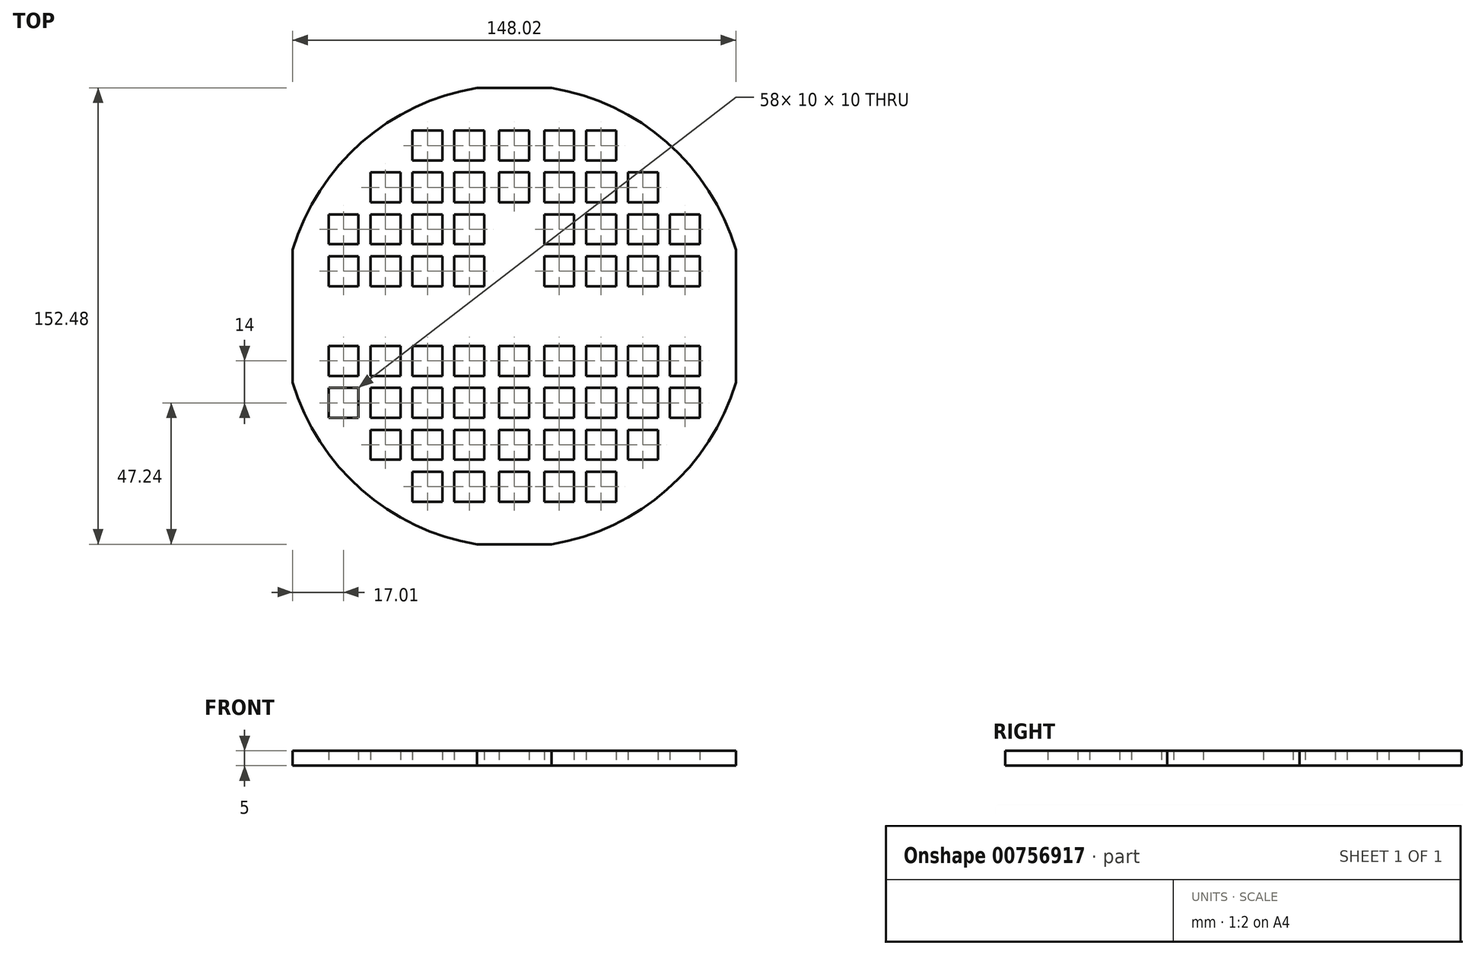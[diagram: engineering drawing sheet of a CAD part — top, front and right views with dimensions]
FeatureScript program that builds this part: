
annotation { "Feature Type Name" : "Feature", "Feature Type Description" : "" }
export const myFeature = defineFeature(function(context is Context, id is Id, definition is map)
    precondition{}
    {
        {
            var Q0;
            Q0=qCreatedBy(makeId("Top.planeOp"),FACE);
            var sketch = newSketch(context, id + "F0", { "sketchPlane" : qUnion([Q0])});
            skArc(sketch, "E0", {"start": v(-74, -22.14) * mm, "mid": v(-51, -58.03) * mm, "end": v(-12.45, -76.24) * mm});
            skLineSegment(sketch, "E1.bottom", {"start": v(10, 20) * mm, "end": v(20, 20) * mm});
            skLineSegment(sketch, "E1.top", {"start": v(10, 10) * mm, "end": v(20, 10) * mm});
            skLineSegment(sketch, "E1.left", {"start": v(10, 20) * mm, "end": v(10, 10) * mm});
            skLineSegment(sketch, "E1.right", {"start": v(20, 20) * mm, "end": v(20, 10) * mm});
            skPoint(sketch, "E1.middle", {"position": v(15, 15) * mm});
            skLineSegment(sketch, "E2.0.1.0", {"start": v(10, 24) * mm, "end": v(20, 24) * mm});
            skLineSegment(sketch, "E2.0.1.1", {"start": v(20, 34) * mm, "end": v(20, 24) * mm});
            skLineSegment(sketch, "E2.0.1.2", {"start": v(10, 34) * mm, "end": v(20, 34) * mm});
            skPoint(sketch, "E2.0.1.3", {"position": v(15, 29) * mm});
            skLineSegment(sketch, "E2.0.1.4", {"start": v(10, 34) * mm, "end": v(10, 24) * mm});
            skLineSegment(sketch, "E2.0.2.0", {"start": v(10, 38) * mm, "end": v(20, 38) * mm});
            skLineSegment(sketch, "E2.0.2.1", {"start": v(20, 48) * mm, "end": v(20, 38) * mm});
            skLineSegment(sketch, "E2.0.2.2", {"start": v(10, 48) * mm, "end": v(20, 48) * mm});
            skPoint(sketch, "E2.0.2.3", {"position": v(15, 43) * mm});
            skLineSegment(sketch, "E2.0.2.4", {"start": v(10, 48) * mm, "end": v(10, 38) * mm});
            skLineSegment(sketch, "E2.0.3.0", {"start": v(10, 52) * mm, "end": v(20, 52) * mm});
            skLineSegment(sketch, "E2.0.3.1", {"start": v(20, 62) * mm, "end": v(20, 52) * mm});
            skLineSegment(sketch, "E2.0.3.2", {"start": v(10, 62) * mm, "end": v(20, 62) * mm});
            skPoint(sketch, "E2.0.3.3", {"position": v(15, 57) * mm});
            skLineSegment(sketch, "E2.0.3.4", {"start": v(10, 62) * mm, "end": v(10, 52) * mm});
            skLineSegment(sketch, "E2.1.0.0", {"start": v(24, 10) * mm, "end": v(34, 10) * mm});
            skLineSegment(sketch, "E2.1.0.1", {"start": v(34, 20) * mm, "end": v(34, 10) * mm});
            skLineSegment(sketch, "E2.1.0.2", {"start": v(24, 20) * mm, "end": v(34, 20) * mm});
            skPoint(sketch, "E2.1.0.3", {"position": v(29, 15) * mm});
            skLineSegment(sketch, "E2.1.0.4", {"start": v(24, 20) * mm, "end": v(24, 10) * mm});
            skLineSegment(sketch, "E2.1.1.0", {"start": v(24, 24) * mm, "end": v(34, 24) * mm});
            skLineSegment(sketch, "E2.1.1.1", {"start": v(34, 34) * mm, "end": v(34, 24) * mm});
            skLineSegment(sketch, "E2.1.1.2", {"start": v(24, 34) * mm, "end": v(34, 34) * mm});
            skPoint(sketch, "E2.1.1.3", {"position": v(29, 29) * mm});
            skLineSegment(sketch, "E2.1.1.4", {"start": v(24, 34) * mm, "end": v(24, 24) * mm});
            skLineSegment(sketch, "E2.1.2.0", {"start": v(24, 38) * mm, "end": v(34, 38) * mm});
            skLineSegment(sketch, "E2.1.2.1", {"start": v(34, 48) * mm, "end": v(34, 38) * mm});
            skLineSegment(sketch, "E2.1.2.2", {"start": v(24, 48) * mm, "end": v(34, 48) * mm});
            skPoint(sketch, "E2.1.2.3", {"position": v(29, 43) * mm});
            skLineSegment(sketch, "E2.1.2.4", {"start": v(24, 48) * mm, "end": v(24, 38) * mm});
            skLineSegment(sketch, "E2.1.3.0", {"start": v(24, 52) * mm, "end": v(34, 52) * mm});
            skLineSegment(sketch, "E2.1.3.1", {"start": v(34, 62) * mm, "end": v(34, 52) * mm});
            skLineSegment(sketch, "E2.1.3.2", {"start": v(24, 62) * mm, "end": v(34, 62) * mm});
            skPoint(sketch, "E2.1.3.3", {"position": v(29, 57) * mm});
            skLineSegment(sketch, "E2.1.3.4", {"start": v(24, 62) * mm, "end": v(24, 52) * mm});
            skLineSegment(sketch, "E2.2.0.0", {"start": v(38, 10) * mm, "end": v(48, 10) * mm});
            skLineSegment(sketch, "E2.2.0.1", {"start": v(48, 20) * mm, "end": v(48, 10) * mm});
            skLineSegment(sketch, "E2.2.0.2", {"start": v(38, 20) * mm, "end": v(48, 20) * mm});
            skPoint(sketch, "E2.2.0.3", {"position": v(43, 15) * mm});
            skLineSegment(sketch, "E2.2.0.4", {"start": v(38, 20) * mm, "end": v(38, 10) * mm});
            skLineSegment(sketch, "E2.2.1.0", {"start": v(38, 24) * mm, "end": v(48, 24) * mm});
            skLineSegment(sketch, "E2.2.1.1", {"start": v(48, 34) * mm, "end": v(48, 24) * mm});
            skLineSegment(sketch, "E2.2.1.2", {"start": v(38, 34) * mm, "end": v(48, 34) * mm});
            skPoint(sketch, "E2.2.1.3", {"position": v(43, 29) * mm});
            skLineSegment(sketch, "E2.2.1.4", {"start": v(38, 34) * mm, "end": v(38, 24) * mm});
            skLineSegment(sketch, "E2.2.2.0", {"start": v(38, 38) * mm, "end": v(48, 38) * mm});
            skLineSegment(sketch, "E2.2.2.1", {"start": v(48, 48) * mm, "end": v(48, 38) * mm});
            skLineSegment(sketch, "E2.2.2.2", {"start": v(38, 48) * mm, "end": v(48, 48) * mm});
            skPoint(sketch, "E2.2.2.3", {"position": v(43, 43) * mm});
            skLineSegment(sketch, "E2.2.2.4", {"start": v(38, 48) * mm, "end": v(38, 38) * mm});
            skLineSegment(sketch, "E2.3.0.0", {"start": v(52, 10) * mm, "end": v(62, 10) * mm});
            skLineSegment(sketch, "E2.3.0.1", {"start": v(62, 20) * mm, "end": v(62, 10) * mm});
            skLineSegment(sketch, "E2.3.0.2", {"start": v(52, 20) * mm, "end": v(62, 20) * mm});
            skPoint(sketch, "E2.3.0.3", {"position": v(57, 15) * mm});
            skLineSegment(sketch, "E2.3.0.4", {"start": v(52, 20) * mm, "end": v(52, 10) * mm});
            skLineSegment(sketch, "E2.3.1.0", {"start": v(52, 24) * mm, "end": v(62, 24) * mm});
            skLineSegment(sketch, "E2.3.1.1", {"start": v(62, 34) * mm, "end": v(62, 24) * mm});
            skLineSegment(sketch, "E2.3.1.2", {"start": v(52, 34) * mm, "end": v(62, 34) * mm});
            skPoint(sketch, "E2.3.1.3", {"position": v(57, 29) * mm});
            skLineSegment(sketch, "E2.3.1.4", {"start": v(52, 34) * mm, "end": v(52, 24) * mm});
            skLineSegment(sketch, "E2.direction1", {"start": v(10, 10) * mm, "end": v(24, 10) * mm, "construction": true});
            skLineSegment(sketch, "E2.direction2", {"start": v(10, 10) * mm, "end": v(10, 24) * mm, "construction": true});
            skLineSegment(sketch, "E3.MirrorCS", {"start": v(34, -20) * mm, "end": v(34, -10) * mm});
            skLineSegment(sketch, "E4.MirrorCS", {"start": v(10, -10) * mm, "end": v(20, -10) * mm});
            skLineSegment(sketch, "E5.MirrorCS", {"start": v(10, -20) * mm, "end": v(10, -10) * mm});
            skLineSegment(sketch, "E6.MirrorCS", {"start": v(48, -20) * mm, "end": v(48, -10) * mm});
            skLineSegment(sketch, "E7.MirrorCS", {"start": v(62, -34) * mm, "end": v(62, -24) * mm});
            skLineSegment(sketch, "E8.MirrorCS", {"start": v(24, -62) * mm, "end": v(34, -62) * mm});
            skLineSegment(sketch, "E9.MirrorCS", {"start": v(48, -34) * mm, "end": v(48, -24) * mm});
            skPoint(sketch, "E10.MirrorP", {"position": v(29, -29) * mm});
            skPoint(sketch, "E11.MirrorP", {"position": v(57, -15) * mm});
            skPoint(sketch, "E12.MirrorP", {"position": v(29, -43) * mm});
            skLineSegment(sketch, "E13.MirrorCS", {"start": v(38, -10) * mm, "end": v(48, -10) * mm});
            skLineSegment(sketch, "E14.MirrorCS", {"start": v(52, -24) * mm, "end": v(62, -24) * mm});
            skLineSegment(sketch, "E15.MirrorCS", {"start": v(24, -34) * mm, "end": v(24, -24) * mm});
            skLineSegment(sketch, "E16.MirrorCS", {"start": v(24, -10) * mm, "end": v(34, -10) * mm});
            skLineSegment(sketch, "E17.MirrorCS", {"start": v(38, -34) * mm, "end": v(38, -24) * mm});
            skLineSegment(sketch, "E18.MirrorCS", {"start": v(24, -48) * mm, "end": v(24, -38) * mm});
            skPoint(sketch, "E19.MirrorP", {"position": v(29, -15) * mm});
            skLineSegment(sketch, "E20.MirrorCS", {"start": v(52, -20) * mm, "end": v(52, -10) * mm});
            skLineSegment(sketch, "E21.MirrorCS", {"start": v(10, -62) * mm, "end": v(10, -52) * mm});
            skPoint(sketch, "E22.MirrorP", {"position": v(15, -57) * mm});
            skPoint(sketch, "E23.MirrorP", {"position": v(57, -29) * mm});
            skPoint(sketch, "E24.MirrorP", {"position": v(15, -15) * mm});
            skLineSegment(sketch, "E25.MirrorCS", {"start": v(10, -20) * mm, "end": v(20, -20) * mm});
            skLineSegment(sketch, "E26.MirrorCS", {"start": v(20, -62) * mm, "end": v(20, -52) * mm});
            skPoint(sketch, "E27.MirrorP", {"position": v(29, -57) * mm});
            skLineSegment(sketch, "E28.MirrorCS", {"start": v(24, -48) * mm, "end": v(34, -48) * mm});
            skLineSegment(sketch, "E29.MirrorCS", {"start": v(10, -52) * mm, "end": v(20, -52) * mm});
            skLineSegment(sketch, "E30.MirrorCS", {"start": v(52, -34) * mm, "end": v(62, -34) * mm});
            skLineSegment(sketch, "E31.MirrorCS", {"start": v(38, -20) * mm, "end": v(48, -20) * mm});
            skLineSegment(sketch, "E32.MirrorCS", {"start": v(24, -20) * mm, "end": v(34, -20) * mm});
            skLineSegment(sketch, "E33.MirrorCS", {"start": v(24, -20) * mm, "end": v(24, -10) * mm});
            skLineSegment(sketch, "E34.MirrorCS", {"start": v(10, -62) * mm, "end": v(20, -62) * mm});
            skLineSegment(sketch, "E35.MirrorCS", {"start": v(52, -10) * mm, "end": v(62, -10) * mm});
            skLineSegment(sketch, "E36.MirrorCS", {"start": v(52, -34) * mm, "end": v(52, -24) * mm});
            skLineSegment(sketch, "E37.MirrorCS", {"start": v(38, -20) * mm, "end": v(38, -10) * mm});
            skLineSegment(sketch, "E38.MirrorCS", {"start": v(24, -52) * mm, "end": v(34, -52) * mm});
            skLineSegment(sketch, "E39.MirrorCS", {"start": v(24, -62) * mm, "end": v(24, -52) * mm});
            skArc(sketch, "E40.MirrorC", {"start": v(-74, 22.14) * mm, "mid": v(-51, 58.03) * mm, "end": v(-12.45, 76.24) * mm});
            skLineSegment(sketch, "E41.MirrorCS", {"start": v(34, -48) * mm, "end": v(34, -38) * mm});
            skPoint(sketch, "E42.MirrorP", {"position": v(43, -15) * mm});
            skPoint(sketch, "E43.MirrorP", {"position": v(15, -29) * mm});
            skLineSegment(sketch, "E44.MirrorCS", {"start": v(48, -48) * mm, "end": v(48, -38) * mm});
            skLineSegment(sketch, "E45.MirrorCS", {"start": v(38, -48) * mm, "end": v(38, -38) * mm});
            skLineSegment(sketch, "E46.MirrorCS", {"start": v(24, -24) * mm, "end": v(34, -24) * mm});
            skLineSegment(sketch, "E47.MirrorCS", {"start": v(10, -10) * mm, "end": v(24, -10) * mm, "construction": true});
            skLineSegment(sketch, "E48.MirrorCS", {"start": v(62, -20) * mm, "end": v(62, -10) * mm});
            skLineSegment(sketch, "E49.MirrorCS", {"start": v(38, -24) * mm, "end": v(48, -24) * mm});
            skLineSegment(sketch, "E50.MirrorCS", {"start": v(20, -20) * mm, "end": v(20, -10) * mm});
            skLineSegment(sketch, "E51.MirrorCS", {"start": v(10, -24) * mm, "end": v(20, -24) * mm});
            skLineSegment(sketch, "E52.MirrorCS", {"start": v(24, -34) * mm, "end": v(34, -34) * mm});
            skLineSegment(sketch, "E53.MirrorCS", {"start": v(20, -34) * mm, "end": v(20, -24) * mm});
            skLineSegment(sketch, "E54.MirrorCS", {"start": v(38, -38) * mm, "end": v(48, -38) * mm});
            skLineSegment(sketch, "E55.MirrorCS", {"start": v(52, -20) * mm, "end": v(62, -20) * mm});
            skLineSegment(sketch, "E56.MirrorCS", {"start": v(34, -62) * mm, "end": v(34, -52) * mm});
            skPoint(sketch, "E57.MirrorP", {"position": v(15, -43) * mm});
            skPoint(sketch, "E58.MirrorP", {"position": v(43, -43) * mm});
            skLineSegment(sketch, "E59.MirrorCS", {"start": v(10, -34) * mm, "end": v(20, -34) * mm});
            skLineSegment(sketch, "E60.MirrorCS", {"start": v(20, -48) * mm, "end": v(20, -38) * mm});
            skLineSegment(sketch, "E61.MirrorCS", {"start": v(38, -34) * mm, "end": v(48, -34) * mm});
            skLineSegment(sketch, "E62.MirrorCS", {"start": v(10, -10) * mm, "end": v(10, -24) * mm, "construction": true});
            skLineSegment(sketch, "E63.MirrorCS", {"start": v(38, -48) * mm, "end": v(48, -48) * mm});
            skLineSegment(sketch, "E64.MirrorCS", {"start": v(10, -34) * mm, "end": v(10, -24) * mm});
            skLineSegment(sketch, "E65.MirrorCS", {"start": v(34, -34) * mm, "end": v(34, -24) * mm});
            skPoint(sketch, "E66.MirrorP", {"position": v(43, -29) * mm});
            skLineSegment(sketch, "E67.MirrorCS", {"start": v(10, -38) * mm, "end": v(20, -38) * mm});
            skLineSegment(sketch, "E68.MirrorCS", {"start": v(10, -48) * mm, "end": v(10, -38) * mm});
            skLineSegment(sketch, "E69.MirrorCS", {"start": v(24, -38) * mm, "end": v(34, -38) * mm});
            skLineSegment(sketch, "E70.MirrorCS", {"start": v(10, -48) * mm, "end": v(20, -48) * mm});
            skLineSegment(sketch, "E71.MirrorCS", {"start": v(-34, 20) * mm, "end": v(-34, 10) * mm});
            skLineSegment(sketch, "E72.MirrorCS", {"start": v(-10, -20) * mm, "end": v(-10, -10) * mm});
            skLineSegment(sketch, "E73.MirrorCS", {"start": v(-10, -10) * mm, "end": v(-20, -10) * mm});
            skLineSegment(sketch, "E74.MirrorCS", {"start": v(-10, 10) * mm, "end": v(-20, 10) * mm});
            skLineSegment(sketch, "E75.MirrorCS", {"start": v(-48, -20) * mm, "end": v(-48, -10) * mm});
            skLineSegment(sketch, "E76.MirrorCS", {"start": v(-10, 20) * mm, "end": v(-10, 10) * mm});
            skLineSegment(sketch, "E77.MirrorCS", {"start": v(-20, -20) * mm, "end": v(-20, -10) * mm});
            skPoint(sketch, "E78.MirrorP", {"position": v(-15, 15) * mm});
            skPoint(sketch, "E79.MirrorP", {"position": v(-29, -15) * mm});
            skLineSegment(sketch, "E80.MirrorCS", {"start": v(-34, -62) * mm, "end": v(-34, -52) * mm});
            skLineSegment(sketch, "E81.MirrorCS", {"start": v(-48, 20) * mm, "end": v(-48, 10) * mm});
            skLineSegment(sketch, "E82.MirrorCS", {"start": v(-62, 34) * mm, "end": v(-62, 24) * mm});
            skLineSegment(sketch, "E83.MirrorCS", {"start": v(-38, -34) * mm, "end": v(-38, -24) * mm});
            skLineSegment(sketch, "E84.MirrorCS", {"start": v(-24, -52) * mm, "end": v(-34, -52) * mm});
            skPoint(sketch, "E85.MirrorP", {"position": v(-43, 29) * mm});
            skPoint(sketch, "E86.MirrorP", {"position": v(-43, -43) * mm});
            skLineSegment(sketch, "E87.MirrorCS", {"start": v(-10, -52) * mm, "end": v(-20, -52) * mm});
            skLineSegment(sketch, "E88.MirrorCS", {"start": v(-10, -10) * mm, "end": v(-24, -10) * mm, "construction": true});
            skLineSegment(sketch, "E89.MirrorCS", {"start": v(-34, -34) * mm, "end": v(-34, -24) * mm});
            skLineSegment(sketch, "E90.MirrorCS", {"start": v(-24, 38) * mm, "end": v(-34, 38) * mm});
            skLineSegment(sketch, "E91.MirrorCS", {"start": v(-38, 38) * mm, "end": v(-48, 38) * mm});
            skLineSegment(sketch, "E92.MirrorCS", {"start": v(-52, -20) * mm, "end": v(-62, -20) * mm});
            skLineSegment(sketch, "E93.MirrorCS", {"start": v(-38, 10) * mm, "end": v(-48, 10) * mm});
            skLineSegment(sketch, "E94.MirrorCS", {"start": v(-52, 24) * mm, "end": v(-62, 24) * mm});
            skLineSegment(sketch, "E95.MirrorCS", {"start": v(-24, -10) * mm, "end": v(-34, -10) * mm});
            skLineSegment(sketch, "E96.MirrorCS", {"start": v(-38, -20) * mm, "end": v(-38, -10) * mm});
            skLineSegment(sketch, "E97.MirrorCS", {"start": v(-24, 10) * mm, "end": v(-34, 10) * mm});
            skPoint(sketch, "E98.MirrorP", {"position": v(-43, 15) * mm});
            skPoint(sketch, "E99.MirrorP", {"position": v(-15, -43) * mm});
            skLineSegment(sketch, "E100.MirrorCS", {"start": v(-24, -48) * mm, "end": v(-34, -48) * mm});
            skLineSegment(sketch, "E101.MirrorCS", {"start": v(-24, -24) * mm, "end": v(-34, -24) * mm});
            skLineSegment(sketch, "E102.MirrorCS", {"start": v(-10, -34) * mm, "end": v(-10, -24) * mm});
            skLineSegment(sketch, "E103.MirrorCS", {"start": v(-24, 34) * mm, "end": v(-24, 24) * mm});
            skLineSegment(sketch, "E104.MirrorCS", {"start": v(-38, 34) * mm, "end": v(-38, 24) * mm});
            skPoint(sketch, "E105.MirrorP", {"position": v(-29, -43) * mm});
            skLineSegment(sketch, "E106.MirrorCS", {"start": v(-24, 62) * mm, "end": v(-24, 52) * mm});
            skLineSegment(sketch, "E107.MirrorCS", {"start": v(-52, 20) * mm, "end": v(-52, 10) * mm});
            skLineSegment(sketch, "E108.MirrorCS", {"start": v(-24, -34) * mm, "end": v(-24, -24) * mm});
            skLineSegment(sketch, "E109.MirrorCS", {"start": v(-52, -34) * mm, "end": v(-52, -24) * mm});
            skLineSegment(sketch, "E110.MirrorCS", {"start": v(-10, 62) * mm, "end": v(-10, 52) * mm});
            skPoint(sketch, "E111.MirrorP", {"position": v(-29, 57) * mm});
            skPoint(sketch, "E112.MirrorP", {"position": v(-15, -29) * mm});
            skLineSegment(sketch, "E113.MirrorCS", {"start": v(-20, -62) * mm, "end": v(-20, -52) * mm});
            skLineSegment(sketch, "E114.MirrorCS", {"start": v(-38, -48) * mm, "end": v(-38, -38) * mm});
            skLineSegment(sketch, "E115.MirrorCS", {"start": v(-38, -48) * mm, "end": v(-48, -48) * mm});
            skLineSegment(sketch, "E116.MirrorCS", {"start": v(-24, 34) * mm, "end": v(-34, 34) * mm});
            skLineSegment(sketch, "E117.MirrorCS", {"start": v(-38, 34) * mm, "end": v(-48, 34) * mm});
            skLineSegment(sketch, "E118.MirrorCS", {"start": v(-34, -20) * mm, "end": v(-34, -10) * mm});
            skPoint(sketch, "E119.MirrorP", {"position": v(-57, -15) * mm});
            skLineSegment(sketch, "E120.MirrorCS", {"start": v(-38, -38) * mm, "end": v(-48, -38) * mm});
            skLineSegment(sketch, "E121.MirrorCS", {"start": v(-10, 48) * mm, "end": v(-10, 38) * mm});
            skLineSegment(sketch, "E122.MirrorCS", {"start": v(-10, 48) * mm, "end": v(-20, 48) * mm});
            skLineSegment(sketch, "E123.MirrorCS", {"start": v(-20, 48) * mm, "end": v(-20, 38) * mm});
            skLineSegment(sketch, "E124.MirrorCS", {"start": v(-10, 38) * mm, "end": v(-20, 38) * mm});
            skLineSegment(sketch, "E125.MirrorCS", {"start": v(-10, 34) * mm, "end": v(-10, 24) * mm});
            skLineSegment(sketch, "E126.MirrorCS", {"start": v(-10, 24) * mm, "end": v(-20, 24) * mm});
            skLineSegment(sketch, "E127.MirrorCS", {"start": v(-10, 20) * mm, "end": v(-20, 20) * mm});
            skLineSegment(sketch, "E128.MirrorCS", {"start": v(-10, 52) * mm, "end": v(-20, 52) * mm});
            skLineSegment(sketch, "E129.MirrorCS", {"start": v(-20, -34) * mm, "end": v(-20, -24) * mm});
            skLineSegment(sketch, "E130.MirrorCS", {"start": v(-10, -10) * mm, "end": v(-10, -24) * mm, "construction": true});
            skLineSegment(sketch, "E131.MirrorCS", {"start": v(-24, 62) * mm, "end": v(-34, 62) * mm});
            skPoint(sketch, "E132.MirrorP", {"position": v(-43, -15) * mm});
            skPoint(sketch, "E133.MirrorP", {"position": v(-43, -29) * mm});
            skLineSegment(sketch, "E134.MirrorCS", {"start": v(-52, -24) * mm, "end": v(-62, -24) * mm});
            skPoint(sketch, "E135.MirrorP", {"position": v(-43, 43) * mm});
            skPoint(sketch, "E136.MirrorP", {"position": v(-29, -29) * mm});
            skLineSegment(sketch, "E137.MirrorCS", {"start": v(-48, 48) * mm, "end": v(-48, 38) * mm});
            skLineSegment(sketch, "E138.MirrorCS", {"start": v(-34, 48) * mm, "end": v(-34, 38) * mm});
            skLineSegment(sketch, "E139.MirrorCS", {"start": v(-10, -38) * mm, "end": v(-20, -38) * mm});
            skLineSegment(sketch, "E140.MirrorCS", {"start": v(-52, -34) * mm, "end": v(-62, -34) * mm});
            skLineSegment(sketch, "E141.MirrorCS", {"start": v(-62, -20) * mm, "end": v(-62, -10) * mm});
            skLineSegment(sketch, "E142.MirrorCS", {"start": v(-24, 20) * mm, "end": v(-34, 20) * mm});
            skLineSegment(sketch, "E143.MirrorCS", {"start": v(-24, -48) * mm, "end": v(-24, -38) * mm});
            skLineSegment(sketch, "E144.MirrorCS", {"start": v(-24, -62) * mm, "end": v(-24, -52) * mm});
            skLineSegment(sketch, "E145.MirrorCS", {"start": v(-38, 20) * mm, "end": v(-48, 20) * mm});
            skLineSegment(sketch, "E146.MirrorCS", {"start": v(-38, 48) * mm, "end": v(-38, 38) * mm});
            skPoint(sketch, "E147.MirrorP", {"position": v(-15, 29) * mm});
            skLineSegment(sketch, "E148.MirrorCS", {"start": v(-20, 62) * mm, "end": v(-20, 52) * mm});
            skLineSegment(sketch, "E149.MirrorCS", {"start": v(-38, -10) * mm, "end": v(-48, -10) * mm});
            skLineSegment(sketch, "E150.MirrorCS", {"start": v(-10, -20) * mm, "end": v(-20, -20) * mm});
            skPoint(sketch, "E151.MirrorP", {"position": v(-15, 57) * mm});
            skLineSegment(sketch, "E152.MirrorCS", {"start": v(-20, -48) * mm, "end": v(-20, -38) * mm});
            skLineSegment(sketch, "E153.MirrorCS", {"start": v(-48, 34) * mm, "end": v(-48, 24) * mm});
            skPoint(sketch, "E154.MirrorP", {"position": v(-15, 43) * mm});
            skPoint(sketch, "E155.MirrorP", {"position": v(-57, -29) * mm});
            skPoint(sketch, "E156.MirrorP", {"position": v(-15, -15) * mm});
            skLineSegment(sketch, "E157.MirrorCS", {"start": v(-20, 34) * mm, "end": v(-20, 24) * mm});
            skLineSegment(sketch, "E158.MirrorCS", {"start": v(-10, -24) * mm, "end": v(-20, -24) * mm});
            skLineSegment(sketch, "E159.MirrorCS", {"start": v(-20, 20) * mm, "end": v(-20, 10) * mm});
            skLineSegment(sketch, "E160.MirrorCS", {"start": v(-10, 10) * mm, "end": v(-10, 24) * mm, "construction": true});
            skLineSegment(sketch, "E161.MirrorCS", {"start": v(-34, 62) * mm, "end": v(-34, 52) * mm});
            skLineSegment(sketch, "E162.MirrorCS", {"start": v(-24, -34) * mm, "end": v(-34, -34) * mm});
            skLineSegment(sketch, "E163.MirrorCS", {"start": v(-38, 24) * mm, "end": v(-48, 24) * mm});
            skLineSegment(sketch, "E164.MirrorCS", {"start": v(-62, 20) * mm, "end": v(-62, 10) * mm});
            skLineSegment(sketch, "E165.MirrorCS", {"start": v(-10, 10) * mm, "end": v(-24, 10) * mm, "construction": true});
            skLineSegment(sketch, "E166.MirrorCS", {"start": v(-10, -34) * mm, "end": v(-20, -34) * mm});
            skPoint(sketch, "E167.MirrorP", {"position": v(-29, 43) * mm});
            skLineSegment(sketch, "E168.MirrorCS", {"start": v(-10, -62) * mm, "end": v(-10, -52) * mm});
            skLineSegment(sketch, "E169.MirrorCS", {"start": v(-10, 34) * mm, "end": v(-20, 34) * mm});
            skPoint(sketch, "E170.MirrorP", {"position": v(-15, -57) * mm});
            skLineSegment(sketch, "E171.MirrorCS", {"start": v(-10, -62) * mm, "end": v(-20, -62) * mm});
            skLineSegment(sketch, "E172.MirrorCS", {"start": v(-10, -48) * mm, "end": v(-20, -48) * mm});
            skLineSegment(sketch, "E173.MirrorCS", {"start": v(-34, -48) * mm, "end": v(-34, -38) * mm});
            skLineSegment(sketch, "E174.MirrorCS", {"start": v(-24, 24) * mm, "end": v(-34, 24) * mm});
            skLineSegment(sketch, "E175.MirrorCS", {"start": v(-24, 52) * mm, "end": v(-34, 52) * mm});
            skLineSegment(sketch, "E176.MirrorCS", {"start": v(-24, -20) * mm, "end": v(-34, -20) * mm});
            skLineSegment(sketch, "E177.MirrorCS", {"start": v(-24, -38) * mm, "end": v(-34, -38) * mm});
            skLineSegment(sketch, "E178.MirrorCS", {"start": v(-24, 48) * mm, "end": v(-24, 38) * mm});
            skLineSegment(sketch, "E179.MirrorCS", {"start": v(-24, -62) * mm, "end": v(-34, -62) * mm});
            skLineSegment(sketch, "E180.MirrorCS", {"start": v(-38, 20) * mm, "end": v(-38, 10) * mm});
            skLineSegment(sketch, "E181.MirrorCS", {"start": v(-52, 34) * mm, "end": v(-62, 34) * mm});
            skLineSegment(sketch, "E182.MirrorCS", {"start": v(-52, 34) * mm, "end": v(-52, 24) * mm});
            skPoint(sketch, "E183.MirrorP", {"position": v(-29, 29) * mm});
            skPoint(sketch, "E184.MirrorP", {"position": v(-57, 29) * mm});
            skLineSegment(sketch, "E185.MirrorCS", {"start": v(-38, -24) * mm, "end": v(-48, -24) * mm});
            skLineSegment(sketch, "E186.MirrorCS", {"start": v(-52, 10) * mm, "end": v(-62, 10) * mm});
            skLineSegment(sketch, "E187.MirrorCS", {"start": v(-48, -34) * mm, "end": v(-48, -24) * mm});
            skLineSegment(sketch, "E188.MirrorCS", {"start": v(-52, -20) * mm, "end": v(-52, -10) * mm});
            skLineSegment(sketch, "E189.MirrorCS", {"start": v(-24, -20) * mm, "end": v(-24, -10) * mm});
            skLineSegment(sketch, "E190.MirrorCS", {"start": v(-24, 20) * mm, "end": v(-24, 10) * mm});
            skLineSegment(sketch, "E191.MirrorCS", {"start": v(-10, 62) * mm, "end": v(-20, 62) * mm});
            skLineSegment(sketch, "E192.MirrorCS", {"start": v(-48, -48) * mm, "end": v(-48, -38) * mm});
            skPoint(sketch, "E193.MirrorP", {"position": v(-29, -57) * mm});
            skLineSegment(sketch, "E194.MirrorCS", {"start": v(-24, 48) * mm, "end": v(-34, 48) * mm});
            skLineSegment(sketch, "E195.MirrorCS", {"start": v(-10, -48) * mm, "end": v(-10, -38) * mm});
            skLineSegment(sketch, "E196.MirrorCS", {"start": v(-38, -20) * mm, "end": v(-48, -20) * mm});
            skLineSegment(sketch, "E197.MirrorCS", {"start": v(-38, -34) * mm, "end": v(-48, -34) * mm});
            skLineSegment(sketch, "E198.MirrorCS", {"start": v(-52, -10) * mm, "end": v(-62, -10) * mm});
            skLineSegment(sketch, "E199.MirrorCS", {"start": v(-62, -34) * mm, "end": v(-62, -24) * mm});
            skLineSegment(sketch, "E200.MirrorCS", {"start": v(-52, 20) * mm, "end": v(-62, 20) * mm});
            skLineSegment(sketch, "E201.MirrorCS", {"start": v(-34, 34) * mm, "end": v(-34, 24) * mm});
            skPoint(sketch, "E202.MirrorP", {"position": v(-29, 15) * mm});
            skPoint(sketch, "E203.MirrorP", {"position": v(-57, 15) * mm});
            skLineSegment(sketch, "E204.MirrorCS", {"start": v(-38, 48) * mm, "end": v(-48, 48) * mm});
            skLineSegment(sketch, "E205.bottom", {"start": v(-5, -10) * mm, "end": v(5, -10) * mm});
            skLineSegment(sketch, "E205.top", {"start": v(-5, -20) * mm, "end": v(5, -20) * mm});
            skLineSegment(sketch, "E205.left", {"start": v(-5, -10) * mm, "end": v(-5, -20) * mm});
            skLineSegment(sketch, "E205.right", {"start": v(5, -10) * mm, "end": v(5, -20) * mm});
            skPoint(sketch, "E205.middle", {"position": v(0, -15) * mm});
            skLineSegment(sketch, "E206.0.2.0", {"start": v(-5, 48) * mm, "end": v(5, 48) * mm});
            skLineSegment(sketch, "E206.0.2.1", {"start": v(5, 48) * mm, "end": v(5, 38) * mm});
            skLineSegment(sketch, "E206.0.2.2", {"start": v(-5, 38) * mm, "end": v(5, 38) * mm});
            skPoint(sketch, "E206.0.2.3", {"position": v(0, 43) * mm});
            skLineSegment(sketch, "E206.0.2.4", {"start": v(-5, 48) * mm, "end": v(-5, 38) * mm});
            skLineSegment(sketch, "E206.0.3.0", {"start": v(-5, 62) * mm, "end": v(5, 62) * mm});
            skLineSegment(sketch, "E206.0.3.1", {"start": v(5, 62) * mm, "end": v(5, 52) * mm});
            skLineSegment(sketch, "E206.0.3.2", {"start": v(-5, 52) * mm, "end": v(5, 52) * mm});
            skPoint(sketch, "E206.0.3.3", {"position": v(0, 57) * mm});
            skLineSegment(sketch, "E206.0.3.4", {"start": v(-5, 62) * mm, "end": v(-5, 52) * mm});
            skLineSegment(sketch, "E207.0.1.0", {"start": v(-5, -34) * mm, "end": v(5, -34) * mm});
            skLineSegment(sketch, "E207.0.1.1", {"start": v(-5, -24) * mm, "end": v(-5, -34) * mm});
            skLineSegment(sketch, "E207.0.1.2", {"start": v(5, -24) * mm, "end": v(5, -34) * mm});
            skLineSegment(sketch, "E207.0.1.3", {"start": v(-5, -24) * mm, "end": v(5, -24) * mm});
            skPoint(sketch, "E207.0.1.4", {"position": v(0, -29) * mm});
            skLineSegment(sketch, "E207.0.2.0", {"start": v(-5, -48) * mm, "end": v(5, -48) * mm});
            skLineSegment(sketch, "E207.0.2.1", {"start": v(-5, -38) * mm, "end": v(-5, -48) * mm});
            skLineSegment(sketch, "E207.0.2.2", {"start": v(5, -38) * mm, "end": v(5, -48) * mm});
            skLineSegment(sketch, "E207.0.2.3", {"start": v(-5, -38) * mm, "end": v(5, -38) * mm});
            skPoint(sketch, "E207.0.2.4", {"position": v(0, -43) * mm});
            skLineSegment(sketch, "E207.0.3.0", {"start": v(-5, -62) * mm, "end": v(5, -62) * mm});
            skLineSegment(sketch, "E207.0.3.1", {"start": v(-5, -52) * mm, "end": v(-5, -62) * mm});
            skLineSegment(sketch, "E207.0.3.2", {"start": v(5, -52) * mm, "end": v(5, -62) * mm});
            skLineSegment(sketch, "E207.0.3.3", {"start": v(-5, -52) * mm, "end": v(5, -52) * mm});
            skPoint(sketch, "E207.0.3.4", {"position": v(0, -57) * mm});
            skLineSegment(sketch, "E207.direction1", {"start": v(-5, -20) * mm, "end": v(50.9, -20) * mm, "construction": true});
            skLineSegment(sketch, "E207.direction2", {"start": v(-5, -20) * mm, "end": v(-5, -34) * mm, "construction": true});
            skLineSegment(sketch, "E208", {"start": v(-74, 22.14) * mm, "end": v(-74, -22.14) * mm});
            skLineSegment(sketch, "E209", {"start": v(74, 22.14) * mm, "end": v(74, -22.14) * mm});
            skLineSegment(sketch, "E210", {"start": v(-12.45, 76.24) * mm, "end": v(12.45, 76.24) * mm});
            skLineSegment(sketch, "E211", {"start": v(12.45, -76.24) * mm, "end": v(-12.45, -76.24) * mm});
            skArc(sketch, "E212.trimOffspring", {"start": v(12.45, -76.24) * mm, "mid": v(51, -58.03) * mm, "end": v(74, -22.14) * mm});
            skArc(sketch, "E213.trimOffspring", {"start": v(74, 22.14) * mm, "mid": v(51, 58.03) * mm, "end": v(12.45, 76.24) * mm});
            skArc(sketch, "E214.trimOffspring", {"start": v(-12.45, 76.24) * mm, "mid": v(-51, 58.03) * mm, "end": v(-74, 22.14) * mm});
            skArc(sketch, "E215.trimOffspring", {"start": v(-12.45, -76.24) * mm, "mid": v(-51, -58.03) * mm, "end": v(-74, -22.14) * mm});
            skSolve(sketch);
        }
        {
            var Q0;
            Q0=makeQuery(id+"F0.imprint","IMPRINT",FACE,{"disambiguationData":[TD([[makeQuery(id+"F0.imprint","IMPRINT",EDGE,{"derivedFrom":sQuery(id+"F0.wireOp",EDGE,"E1.bottom")}),1.0]])]});
            extrude(context, id + "F1", {"entities" : qUnion([Q0]), "depth" : 5 * mm, "offsetDistance" : 25 * mm});
        }
    });
